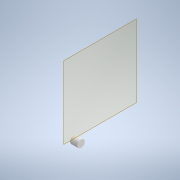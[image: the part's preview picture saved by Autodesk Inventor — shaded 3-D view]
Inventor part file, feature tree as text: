
AUTODESK INVENTOR PART (.ipt)
format: ipt  version: 2022 (Build 260153000, 153)  size: 98,816 bytes
history: native  units: mm
features: other x4, extrude x1, sketch x1
ambient origin geometry x8: Origin, YZ Plane, XZ Plane, XY Plane, X Axis, Y Axis, Z Axis, Center Point
bodies: Body1 (feature_tree)
feature tree (6):
  other  "솔리드1"
  extrude  "돌출1"  Depth=1.0mm
  other  "작업 평면2"
  sketch  "스케치1"
  other  "조립품1"
  other  "큰 원통:1"
